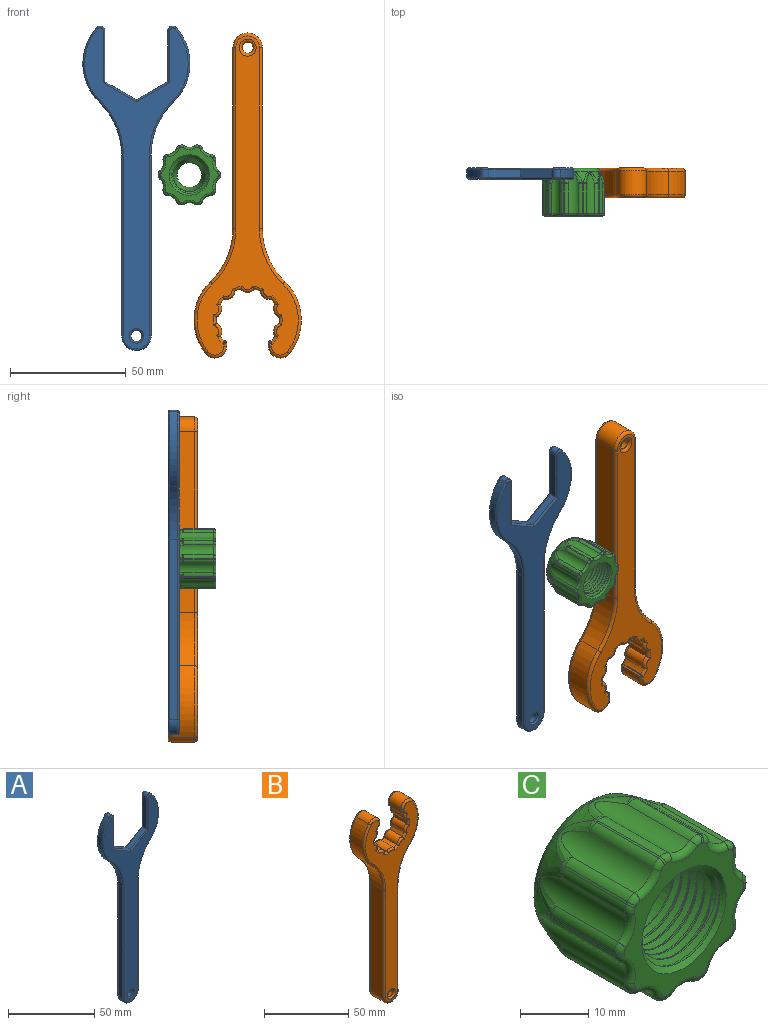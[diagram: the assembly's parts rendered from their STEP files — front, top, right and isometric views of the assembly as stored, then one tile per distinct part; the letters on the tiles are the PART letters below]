
ASSEMBLY  parts=3 mates=2
PART A: 44 faces, bbox 50x4.8x141.1 mm
  f0: cylinder r=6.35mm len=12.7mm, axis (0,1,0), area 64.9mm2, adj f9,f10,f24,f30
  f1: cylinder r=23.09mm len=32.12mm, axis (0,-1,0), area 115.6mm2, adj f12,f14,f27,f36
  f2: plane 21.98x3.25mm, normal (-1,0,0), area 71.5mm2, adj f6,f14,f23,f40
  f3: cylinder r=23.09mm len=32.12mm, axis (0,-1,0), area 115.6mm2, adj f11,f15,f18,f35
  f4: plane 21.98x3.25mm, normal (1,0,0), area 71.5mm2, adj f5,f15,f17,f39
  f5: plane 13.56x7.83mm, normal (0.5,0,0.87), area 50.9mm2, adj f4,f6,f19,f41
  f6: plane 13.56x7.83mm, normal (-0.5,0,0.87), area 50.9mm2, adj f2,f5,f21,f42
  f7: plane 138.45x44.65mm, normal (0,1,0), area 1775mm2, adj f30,f31,f32,f33,f34,f35,f36,f37
  f8: plane 138.45x44.65mm, normal (0,-1,0), area 1775mm2, adj f16,f17,f18,f19,f20,f21,f22,f23
  f9: plane 78.01x3.25mm, normal (1,0,0), area 253.6mm2, adj f0,f12,f26,f32
  f10: plane 78.01x3.25mm, normal (-1,0,0), area 253.6mm2, adj f0,f11,f22,f31
  f11: cylinder r=31.75mm len=22.84mm, axis (0,-1,0), area 82.9mm2, adj f3,f10,f20,f33
  f12: cylinder r=31.75mm len=22.84mm, axis (0,-1,0), area 82.9mm2, adj f1,f9,f28,f34
  f13: cylinder r=2.39mm len=4.78mm, axis (0,1,0), area 48.8mm2, adj f29,f43
  f14: cylinder r=2.03mm len=3.54mm, axis (0,-1,0), area 15.9mm2, adj f1,f2,f25,f38
  f15: cylinder r=2.03mm len=3.54mm, axis (0,-1,0), area 15.9mm2, adj f3,f4,f16,f37
  f16: torus R=1.27mm, axis (0,1,0), area 5.1mm2, adj f8,f15,f17,f18
  f17: cylinder r=0.76mm len=22.42mm, axis (0,0,-1), area 26.5mm2, adj f4,f8,f16,f19
  f18: torus R=22.33mm, axis (0,1,0), area 42mm2, adj f3,f8,f16,f20
  f19: cylinder r=0.76mm len=14.71mm, axis (0.87,0,-0.5), area 19.1mm2, adj f5,f8,f17,f21
  f20: torus R=32.51mm, axis (0,1,0), area 30.8mm2, adj f8,f11,f18,f22
  f21: cylinder r=0.76mm len=14.71mm, axis (0.87,0,0.5), area 19.1mm2, adj f6,f8,f19,f23
  f22: cylinder r=0.76mm len=78.01mm, axis (0,0,-1), area 93.4mm2, adj f8,f10,f20,f24
  f23: cylinder r=0.76mm len=22.42mm, axis (0,0,1), area 26.5mm2, adj f2,f8,f21,f25
  f24: torus R=5.59mm, axis (0,1,0), area 22.8mm2, adj f0,f8,f22,f26
  f25: torus R=1.27mm, axis (0,1,0), area 5.1mm2, adj f8,f14,f23,f27
  f26: cylinder r=0.76mm len=78.01mm, axis (0,0,1), area 93.4mm2, adj f8,f9,f24,f28
  f27: torus R=22.33mm, axis (0,1,0), area 42mm2, adj f1,f8,f25,f28
  f28: torus R=32.51mm, axis (0,1,0), area 30.8mm2, adj f8,f12,f26,f27
  f29: torus R=3.15mm, axis (0,1,0), area 20mm2, adj f8,f13
  f30: torus R=5.59mm, axis (0,1,0), area 22.8mm2, adj f0,f7,f31,f32
  f31: cylinder r=0.76mm len=78.01mm, axis (0,0,1), area 93.4mm2, adj f7,f10,f30,f33
  f32: cylinder r=0.76mm len=78.01mm, axis (0,0,-1), area 93.4mm2, adj f7,f9,f30,f34
  f33: torus R=32.51mm, axis (0,1,0), area 30.8mm2, adj f7,f11,f31,f35
  f34: torus R=32.51mm, axis (0,1,0), area 30.8mm2, adj f7,f12,f32,f36
  f35: torus R=22.33mm, axis (0,1,0), area 42mm2, adj f3,f7,f33,f37
  f36: torus R=22.33mm, axis (0,1,0), area 42mm2, adj f1,f7,f34,f38
  f37: torus R=1.27mm, axis (0,1,0), area 5.1mm2, adj f7,f15,f35,f39
  f38: torus R=1.27mm, axis (0,1,0), area 5.1mm2, adj f7,f14,f36,f40
  f39: cylinder r=0.76mm len=22.42mm, axis (0,0,1), area 26.5mm2, adj f4,f7,f37,f41
  f40: cylinder r=0.76mm len=22.42mm, axis (0,0,-1), area 26.5mm2, adj f2,f7,f38,f42
  f41: cylinder r=0.76mm len=14.71mm, axis (-0.87,0,0.5), area 19.1mm2, adj f5,f7,f39,f42
  f42: cylinder r=0.76mm len=14.71mm, axis (-0.87,0,-0.5), area 19.1mm2, adj f6,f7,f40,f41
  f43: torus R=3.15mm, axis (0,1,0), area 20mm2, adj f7,f13
PART B: 95 faces, bbox 50x12.7x141.1 mm
  f0: cylinder r=6.35mm len=12.7mm, axis (0,1,0), area 202.7mm2, adj f28,f29,f59,f90
  f1: cylinder r=23.11mm len=31.01mm, axis (0,-1,0), area 346.2mm2, adj f26,f31,f60,f84
  f2: plane 137.58x43.69mm, normal (0,1,0), area 1709.6mm2, adj f33,f34,f35,f36,f37,f38,f39,f40
  f3: plane 137.58x43.69mm, normal (0,-1,0), area 1709.6mm2, adj f64,f65,f66,f67,f68,f69,f70,f71
  f4: cylinder r=23.11mm len=31.01mm, axis (0,-1,0), area 346.2mm2, adj f27,f30,f53,f91
  f5: cylinder r=13.59mm len=10.16mm, axis (0,-1,0), area 27.1mm2, adj f6,f21,f42,f66
  f6: cylinder r=3.91mm len=10.16mm, axis (0,-1,0), area 66.8mm2, adj f5,f7,f40,f64
  f7: cylinder r=13.59mm len=10.16mm, axis (0,-1,0), area 27.1mm2, adj f6,f8,f38,f65
  f8: cylinder r=3.91mm len=10.16mm, axis (0,-1,0), area 66.8mm2, adj f7,f9,f36,f67
  f9: cylinder r=13.59mm len=10.16mm, axis (0,-1,0), area 27.1mm2, adj f8,f10,f34,f69
  f10: cylinder r=3.91mm len=10.16mm, axis (0,-1,0), area 66.8mm2, adj f9,f11,f33,f71
  f11: cylinder r=13.59mm len=10.16mm, axis (0,-1,0), area 27.1mm2, adj f10,f12,f35,f73
  f12: cylinder r=3.91mm len=10.16mm, axis (0,-1,0), area 66.8mm2, adj f11,f13,f37,f75
  f13: cylinder r=13.59mm len=10.16mm, axis (0,-1,0), area 27.1mm2, adj f12,f14,f39,f77
  f14: cylinder r=3.91mm len=10.16mm, axis (0,-1,0), area 66.8mm2, adj f13,f15,f41,f79
  f15: cylinder r=13.59mm len=10.16mm, axis (0,-1,0), area 27.1mm2, adj f14,f16,f43,f81
  f16: cylinder r=3.91mm len=10.16mm, axis (0,-1,0), area 5.9mm2, adj f15,f25,f45,f83
  f17: cylinder r=3.91mm len=10.16mm, axis (0,-1,0), area 5.9mm2, adj f18,f24,f52,f76
  f18: cylinder r=13.59mm len=10.16mm, axis (0,-1,0), area 27.1mm2, adj f17,f19,f50,f74
  f19: cylinder r=3.91mm len=10.16mm, axis (0,-1,0), area 66.8mm2, adj f18,f20,f48,f72
  f20: cylinder r=13.59mm len=10.16mm, axis (0,-1,0), area 27.1mm2, adj f19,f21,f46,f70
  f21: cylinder r=3.91mm len=10.16mm, axis (0,-1,0), area 66.8mm2, adj f5,f20,f44,f68
  f22: plane 10.16x1.76mm, normal (-1,0,0), area 17.9mm2, adj f24,f26,f56,f80
  f23: plane 10.16x1.76mm, normal (1,0,0), area 17.9mm2, adj f25,f27,f49,f87
  f24: cylinder r=0.51mm len=10.16mm, axis (0,-1,0), area 8.4mm2, adj f17,f22,f54,f78
  f25: cylinder r=0.51mm len=10.16mm, axis (0,-1,0), area 8.4mm2, adj f16,f23,f47,f85
  f26: cylinder r=5.08mm len=10.16mm, axis (0,-1,0), area 127.5mm2, adj f1,f22,f58,f82
  f27: cylinder r=5.08mm len=10.16mm, axis (0,-1,0), area 127.5mm2, adj f4,f23,f51,f89
  f28: plane 78x10.16mm, normal (1,0,0), area 792.5mm2, adj f0,f31,f61,f88
  f29: plane 78x10.16mm, normal (-1,0,0), area 792.5mm2, adj f0,f30,f57,f92
  f30: cylinder r=31.75mm len=22.85mm, axis (0,-1,0), area 259.1mm2, adj f4,f29,f55,f93
  f31: cylinder r=31.75mm len=22.85mm, axis (0,-1,0), area 259.1mm2, adj f1,f28,f62,f86
  f32: cylinder r=2.39mm len=10.16mm, axis (0,1,0), area 152.4mm2, adj f63,f94
  f33: torus R=2.64mm, axis (0,1,0), area 12.6mm2, adj f2,f10,f34,f35
  f34: torus R=14.86mm, axis (0,1,0), area 6.7mm2, adj f2,f9,f33,f36
  f35: torus R=14.86mm, axis (0,1,0), area 6.7mm2, adj f2,f11,f33,f37
  f36: torus R=2.64mm, axis (0,1,0), area 12.6mm2, adj f2,f8,f34,f38
  f37: torus R=2.64mm, axis (0,1,0), area 12.6mm2, adj f2,f12,f35,f39
  f38: torus R=14.86mm, axis (0,1,0), area 6.7mm2, adj f2,f7,f36,f40
  f39: torus R=14.86mm, axis (0,1,0), area 6.7mm2, adj f2,f13,f37,f41
  f40: torus R=2.64mm, axis (0,1,0), area 12.6mm2, adj f2,f6,f38,f42
  f41: torus R=2.64mm, axis (0,1,0), area 12.6mm2, adj f2,f14,f39,f43
  f42: torus R=14.86mm, axis (0,1,0), area 6.7mm2, adj f2,f5,f40,f44
  f43: torus R=14.86mm, axis (0,1,0), area 6.7mm2, adj f2,f15,f41,f45
  f44: torus R=2.64mm, axis (0,1,0), area 12.6mm2, adj f2,f21,f42,f46
  f45: torus R=2.64mm, axis (0,1,0), area 0.9mm2, adj f2,f16,f43,f47
  f46: torus R=14.86mm, axis (0,1,0), area 6.7mm2, adj f2,f20,f44,f48
  f47: bspline ~1.58x1.49mm, area 1.2mm2, adj f25,f45,f49
  f48: torus R=2.64mm, axis (0,1,0), area 12.6mm2, adj f2,f19,f46,f50
  f49: cylinder r=1.27mm len=1.76mm, axis (0,0,-1), area 2.9mm2, adj f2,f23,f47,f51
  f50: torus R=14.86mm, axis (0,1,0), area 6.7mm2, adj f2,f18,f48,f52
  f51: torus R=3.81mm, axis (0,1,0), area 22.8mm2, adj f2,f27,f49,f53
  f52: torus R=2.64mm, axis (0,1,0), area 0.9mm2, adj f2,f17,f50,f54
  f53: torus R=21.84mm, axis (0,1,0), area 66.6mm2, adj f2,f4,f51,f55
  f54: bspline ~1.58x1.49mm, area 1.2mm2, adj f24,f52,f56
  f55: torus R=33.02mm, axis (0,1,0), area 51.6mm2, adj f2,f30,f53,f57
  f56: cylinder r=1.27mm len=1.76mm, axis (0,0,1), area 2.9mm2, adj f2,f22,f54,f58
  f57: cylinder r=1.27mm len=78mm, axis (0,0,1), area 155.6mm2, adj f2,f29,f55,f59
  f58: torus R=3.81mm, axis (0,1,0), area 22.8mm2, adj f2,f26,f56,f60
  f59: torus R=5.08mm, axis (0,1,0), area 36.9mm2, adj f0,f2,f57,f61
  f60: torus R=21.84mm, axis (0,1,0), area 66.6mm2, adj f1,f2,f58,f62
  f61: cylinder r=1.27mm len=78mm, axis (0,0,-1), area 155.6mm2, adj f2,f28,f59,f62
  f62: torus R=33.02mm, axis (0,1,0), area 51.6mm2, adj f2,f31,f60,f61
  f63: torus R=3.66mm, axis (0,1,0), area 35.7mm2, adj f2,f32
  f64: torus R=2.64mm, axis (0,1,0), area 12.6mm2, adj f3,f6,f65,f66
  f65: torus R=14.86mm, axis (0,1,0), area 6.7mm2, adj f3,f7,f64,f67
  f66: torus R=14.86mm, axis (0,1,0), area 6.7mm2, adj f3,f5,f64,f68
  f67: torus R=2.64mm, axis (0,1,0), area 12.6mm2, adj f3,f8,f65,f69
  f68: torus R=2.64mm, axis (0,1,0), area 12.6mm2, adj f3,f21,f66,f70
  f69: torus R=14.86mm, axis (0,1,0), area 6.7mm2, adj f3,f9,f67,f71
  f70: torus R=14.86mm, axis (0,1,0), area 6.7mm2, adj f3,f20,f68,f72
  f71: torus R=2.64mm, axis (0,1,0), area 12.6mm2, adj f3,f10,f69,f73
  f72: torus R=2.64mm, axis (0,1,0), area 12.6mm2, adj f3,f19,f70,f74
  f73: torus R=14.86mm, axis (0,1,0), area 6.7mm2, adj f3,f11,f71,f75
  f74: torus R=14.86mm, axis (0,1,0), area 6.7mm2, adj f3,f18,f72,f76
  f75: torus R=2.64mm, axis (0,1,0), area 12.6mm2, adj f3,f12,f73,f77
  f76: torus R=2.64mm, axis (0,1,0), area 0.9mm2, adj f3,f17,f74,f78
  f77: torus R=14.86mm, axis (0,1,0), area 6.7mm2, adj f3,f13,f75,f79
  f78: bspline ~1.58x1.49mm, area 1.2mm2, adj f24,f76,f80
  f79: torus R=2.64mm, axis (0,1,0), area 12.6mm2, adj f3,f14,f77,f81
  f80: cylinder r=1.27mm len=1.76mm, axis (0,0,-1), area 2.9mm2, adj f3,f22,f78,f82
  f81: torus R=14.86mm, axis (0,1,0), area 6.7mm2, adj f3,f15,f79,f83
  f82: torus R=3.81mm, axis (0,1,0), area 22.8mm2, adj f3,f26,f80,f84
  f83: torus R=2.64mm, axis (0,1,0), area 0.9mm2, adj f3,f16,f81,f85
  f84: torus R=21.84mm, axis (0,1,0), area 66.6mm2, adj f1,f3,f82,f86
  f85: bspline ~1.58x1.49mm, area 1.2mm2, adj f25,f83,f87
  f86: torus R=33.02mm, axis (0,1,0), area 51.6mm2, adj f3,f31,f84,f88
  f87: cylinder r=1.27mm len=1.76mm, axis (0,0,1), area 2.9mm2, adj f3,f23,f85,f89
  f88: cylinder r=1.27mm len=78mm, axis (0,0,1), area 155.6mm2, adj f3,f28,f86,f90
  f89: torus R=3.81mm, axis (0,1,0), area 22.8mm2, adj f3,f27,f87,f91
  f90: torus R=5.08mm, axis (0,1,0), area 36.9mm2, adj f0,f3,f88,f92
  f91: torus R=21.84mm, axis (0,1,0), area 66.6mm2, adj f3,f4,f89,f93
  f92: cylinder r=1.27mm len=78mm, axis (0,0,-1), area 155.6mm2, adj f3,f29,f90,f93
  f93: torus R=33.02mm, axis (0,1,0), area 51.6mm2, adj f3,f30,f91,f92
  f94: torus R=3.66mm, axis (0,1,0), area 35.7mm2, adj f3,f32
PART C: 135 faces, bbox 28.6x21.1x27.8 mm
  f0: cylinder r=13.46mm len=12.87mm, axis (0,-1,0), area 4.8mm2, adj f9,f74,f83,f100
  f1: cylinder r=13.46mm len=12.87mm, axis (0,-1,0), area 4.8mm2, adj f10,f79,f88,f95
  f2: cylinder r=13.46mm len=12.87mm, axis (0,-1,0), area 4.8mm2, adj f11,f84,f89,f103
  f3: cylinder r=13.46mm len=12.87mm, axis (0,-1,0), area 4.8mm2, adj f12,f48,f93,f111
  f4: cylinder r=13.46mm len=12.87mm, axis (0,-1,0), area 4.8mm2, adj f13,f49,f58,f127
  f5: cylinder r=13.46mm len=12.87mm, axis (0,-1,0), area 4.8mm2, adj f14,f44,f53,f119
  f6: cylinder r=13.46mm len=12.87mm, axis (0,-1,0), area 4.8mm2, adj f15,f64,f73,f116
  f7: cylinder r=13.46mm len=12.87mm, axis (0,-1,0), area 4.8mm2, adj f16,f59,f68,f124
  f8: cylinder r=13.46mm len=12.87mm, axis (0,-1,0), area 4.8mm2, adj f17,f54,f63,f132
  f9: torus R=11.18mm, axis (0,1,0), area 0.3mm2, adj f0,f31,f75,f82
  f10: torus R=11.18mm, axis (0,1,0), area 0.3mm2, adj f1,f31,f80,f87
  f11: torus R=11.18mm, axis (0,1,0), area 0.3mm2, adj f2,f31,f85,f90
  f12: torus R=11.18mm, axis (0,1,0), area 0.3mm2, adj f3,f31,f47,f92
  f13: torus R=11.18mm, axis (0,1,0), area 0.3mm2, adj f4,f31,f50,f57
  f14: torus R=11.18mm, axis (0,1,0), area 0.3mm2, adj f5,f31,f45,f52
  f15: torus R=11.18mm, axis (0,1,0), area 0.3mm2, adj f6,f31,f65,f72
  f16: torus R=11.18mm, axis (0,1,0), area 0.3mm2, adj f7,f31,f60,f67
  f17: torus R=11.18mm, axis (0,1,0), area 0.3mm2, adj f8,f31,f55,f62
  f18: plane 16.9x16.9mm, normal (0,1,0), area 26.3mm2, adj f19,f27,f28,f29,f30
  f19: cylinder r=7.22mm len=14.43mm, axis (0,1,0), area 48.6mm2, adj f18,f21,f28,f30
  f20: cone r=8.74mm half-angle=45deg, axis (0,-1,0), area 73.6mm2, adj f21,f24,f28,f29,f30
  f21: cone r=8.74mm half-angle=45deg, axis (0,-1,0), area 1.9mm2, adj f19,f20,f30
  f22: cylinder r=13.46mm len=12.87mm, axis (0,-1,0), area 4.8mm2, adj f32,f69,f78,f108
  f23: plane 19.1x19.1mm, normal (0,1,0), area 171.9mm2, adj f33,f134
  f24: plane 24.89x23.87mm, normal (0,-1,0), area 178.8mm2, adj f20,f94,f95,f96,f97,f98,f99,f100
  f25: cone r=7.05mm half-angle=20deg, axis (0,-1,0), area 196.3mm2, adj f26,f134
  f26: plane 16.46x16.46mm, normal (0,-1,0), area 56.6mm2, adj f25,f27
  f27: cylinder r=8.23mm len=16.46mm, axis (0,1,0), area 247mm2, adj f18,f26
  f28: bspline ~16.15x16.15mm, area 270.5mm2, adj f18,f19,f20,f29
  f29: bspline ~16.15x16.15mm, area 120mm2, adj f18,f20,f28,f30
  f30: bspline ~16.13x16.13mm, area 271.5mm2, adj f18,f19,f20,f21,f29
  f31: cone r=11.15mm half-angle=20deg, axis (0,-1,0), area 132.4mm2, adj f9,f10,f11,f12,f13,f14,f15,f16
  f32: torus R=11.18mm, axis (0,1,0), area 0.3mm2, adj f22,f31,f70,f77
  f33: torus R=9.55mm, axis (0,1,0), area 189.2mm2, adj f23,f31
  f34: cylinder r=3.97mm len=17.19mm, axis (0,-1,0), area 74.6mm2, adj f69,f70,f71,f72,f73,f112
  f35: cylinder r=3.97mm len=17.19mm, axis (0,-1,0), area 74.6mm2, adj f54,f55,f56,f57,f58,f131
  f36: cylinder r=3.97mm len=17.19mm, axis (0,-1,0), area 74.6mm2, adj f59,f60,f61,f62,f63,f128
  f37: cylinder r=3.97mm len=17.19mm, axis (0,-1,0), area 74.6mm2, adj f64,f65,f66,f67,f68,f120
  f38: cylinder r=3.97mm len=17.19mm, axis (0,-1,0), area 74.6mm2, adj f44,f45,f46,f47,f48,f115
  f39: cylinder r=3.97mm len=17.19mm, axis (0,-1,0), area 74.6mm2, adj f49,f50,f51,f52,f53,f123
  f40: cylinder r=3.97mm len=17.19mm, axis (0,-1,0), area 74.6mm2, adj f89,f90,f91,f92,f93,f107
  f41: cylinder r=3.97mm len=17.19mm, axis (0,-1,0), area 74.6mm2, adj f84,f85,f86,f87,f88,f99
  f42: cylinder r=3.97mm len=17.19mm, axis (0,-1,0), area 74.6mm2, adj f79,f80,f81,f82,f83,f96
  f43: cylinder r=3.97mm len=17.19mm, axis (0,-1,0), area 74.6mm2, adj f74,f75,f76,f77,f78,f104
  f44: cylinder r=2.03mm len=12.87mm, axis (0,1,0), area 23.5mm2, adj f5,f38,f45,f117
  f45: bspline ~1.65x1.35mm, area 0.9mm2, adj f14,f38,f44,f46
  f46: bspline ~7.52x6.8mm, area 14.6mm2, adj f31,f38,f45,f47
  f47: bspline ~1.65x1.6mm, area 0.9mm2, adj f12,f38,f46,f48
  f48: cylinder r=2.03mm len=12.87mm, axis (0,1,0), area 23.5mm2, adj f3,f38,f47,f113
  f49: cylinder r=2.03mm len=12.87mm, axis (0,1,0), area 23.5mm2, adj f4,f39,f50,f125
  f50: bspline ~1.77x1.65mm, area 0.9mm2, adj f13,f39,f49,f51
  f51: bspline ~9.3x6.8mm, area 14.6mm2, adj f31,f39,f50,f52
  f52: bspline ~1.77x1.33mm, area 0.9mm2, adj f14,f39,f51,f53
  f53: cylinder r=2.03mm len=12.87mm, axis (0,1,0), area 23.5mm2, adj f5,f39,f52,f121
  f54: cylinder r=2.03mm len=12.87mm, axis (0,1,0), area 23.5mm2, adj f8,f35,f55,f133
  f55: bspline ~1.65x1.6mm, area 0.9mm2, adj f17,f35,f54,f56
  f56: bspline ~7.32x6.8mm, area 14.6mm2, adj f31,f35,f55,f57
  f57: bspline ~1.35x1.33mm, area 0.9mm2, adj f13,f35,f56,f58
  f58: cylinder r=2.03mm len=12.87mm, axis (0,1,0), area 23.5mm2, adj f4,f35,f57,f129
  f59: cylinder r=2.03mm len=12.87mm, axis (0,1,0), area 23.5mm2, adj f7,f36,f60,f126
  f60: bspline ~1.65x1.6mm, area 0.9mm2, adj f16,f36,f59,f61
  f61: bspline ~8.46x6.8mm, area 14.6mm2, adj f31,f36,f60,f62
  f62: bspline ~1.77x1.33mm, area 0.9mm2, adj f17,f36,f61,f63
  f63: cylinder r=2.03mm len=12.87mm, axis (0,1,0), area 23.5mm2, adj f8,f36,f62,f130
  f64: cylinder r=2.03mm len=12.87mm, axis (0,1,0), area 23.5mm2, adj f6,f37,f65,f118
  f65: bspline ~1.77x1.65mm, area 0.9mm2, adj f15,f37,f64,f66
  f66: bspline ~8.24x6.8mm, area 14.6mm2, adj f31,f37,f65,f67
  f67: bspline ~1.65x1.6mm, area 0.9mm2, adj f16,f37,f66,f68
  f68: cylinder r=2.03mm len=12.87mm, axis (0,1,0), area 23.5mm2, adj f7,f37,f67,f122
  f69: cylinder r=2.03mm len=12.87mm, axis (0,1,0), area 23.5mm2, adj f22,f34,f70,f110
  f70: bspline ~1.65x1.35mm, area 0.9mm2, adj f32,f34,f69,f71
  f71: bspline ~7.32x6.8mm, area 14.6mm2, adj f31,f34,f70,f72
  f72: bspline ~1.6x1.33mm, area 0.9mm2, adj f15,f34,f71,f73
  f73: cylinder r=2.03mm len=12.87mm, axis (0,1,0), area 23.5mm2, adj f6,f34,f72,f114
  f74: cylinder r=2.03mm len=12.87mm, axis (0,1,0), area 23.5mm2, adj f0,f43,f75,f102
  f75: bspline ~1.77x1.65mm, area 0.9mm2, adj f9,f43,f74,f76
  f76: bspline ~9.3x6.8mm, area 14.6mm2, adj f31,f43,f75,f77
  f77: bspline ~1.77x1.33mm, area 0.9mm2, adj f32,f43,f76,f78
  f78: cylinder r=2.03mm len=12.87mm, axis (0,1,0), area 23.5mm2, adj f22,f43,f77,f106
  f79: cylinder r=2.03mm len=12.87mm, axis (0,1,0), area 23.5mm2, adj f1,f42,f80,f94
  f80: bspline ~1.65x1.6mm, area 0.9mm2, adj f10,f42,f79,f81
  f81: bspline ~7.52x6.8mm, area 14.6mm2, adj f31,f42,f80,f82
  f82: bspline ~1.35x1.33mm, area 0.9mm2, adj f9,f42,f81,f83
  f83: cylinder r=2.03mm len=12.87mm, axis (0,1,0), area 23.5mm2, adj f0,f42,f82,f98
  f84: cylinder r=2.03mm len=12.87mm, axis (0,1,0), area 23.5mm2, adj f2,f41,f85,f101
  f85: bspline ~1.65x1.6mm, area 0.9mm2, adj f11,f41,f84,f86
  f86: bspline ~8.84x6.8mm, area 14.6mm2, adj f31,f41,f85,f87
  f87: bspline ~1.77x1.33mm, area 0.9mm2, adj f10,f41,f86,f88
  f88: cylinder r=2.03mm len=12.87mm, axis (0,1,0), area 23.5mm2, adj f1,f41,f87,f97
  f89: cylinder r=2.03mm len=12.87mm, axis (0,1,0), area 23.5mm2, adj f2,f40,f90,f105
  f90: bspline ~1.6x1.33mm, area 0.9mm2, adj f11,f40,f89,f91
  f91: bspline ~8.84x6.8mm, area 14.6mm2, adj f31,f40,f90,f92
  f92: bspline ~1.77x1.65mm, area 0.9mm2, adj f12,f40,f91,f93
  f93: cylinder r=2.03mm len=12.87mm, axis (0,1,0), area 23.5mm2, adj f3,f40,f92,f109
  f94: torus R=1.02mm, axis (0,1,0), area 2.4mm2, adj f24,f79,f95,f96
  f95: torus R=12.45mm, axis (0,1,0), area 0.6mm2, adj f1,f24,f94,f97
  f96: torus R=4.98mm, axis (0,1,0), area 8.3mm2, adj f24,f42,f94,f98
  f97: torus R=1.02mm, axis (0,1,0), area 2.4mm2, adj f24,f88,f95,f99
  f98: torus R=1.02mm, axis (0,1,0), area 2.4mm2, adj f24,f83,f96,f100
  f99: torus R=4.98mm, axis (0,1,0), area 8.3mm2, adj f24,f41,f97,f101
  f100: torus R=12.45mm, axis (0,1,0), area 0.6mm2, adj f0,f24,f98,f102
  f101: torus R=1.02mm, axis (0,1,0), area 2.4mm2, adj f24,f84,f99,f103
  f102: torus R=1.02mm, axis (0,1,0), area 2.4mm2, adj f24,f74,f100,f104
  f103: torus R=12.45mm, axis (0,1,0), area 0.6mm2, adj f2,f24,f101,f105
  f104: torus R=4.98mm, axis (0,1,0), area 8.3mm2, adj f24,f43,f102,f106
  f105: torus R=1.02mm, axis (0,1,0), area 2.4mm2, adj f24,f89,f103,f107
  f106: torus R=1.02mm, axis (0,1,0), area 2.4mm2, adj f24,f78,f104,f108
  f107: torus R=4.98mm, axis (0,1,0), area 8.3mm2, adj f24,f40,f105,f109
  f108: torus R=12.45mm, axis (0,1,0), area 0.6mm2, adj f22,f24,f106,f110
  f109: torus R=1.02mm, axis (0,1,0), area 2.4mm2, adj f24,f93,f107,f111
  f110: torus R=1.02mm, axis (0,1,0), area 2.4mm2, adj f24,f69,f108,f112
  f111: torus R=12.45mm, axis (0,1,0), area 0.6mm2, adj f3,f24,f109,f113
  f112: torus R=4.98mm, axis (0,1,0), area 8.3mm2, adj f24,f34,f110,f114
  f113: torus R=1.02mm, axis (0,1,0), area 2.4mm2, adj f24,f48,f111,f115
  f114: torus R=1.02mm, axis (0,1,0), area 2.4mm2, adj f24,f73,f112,f116
  f115: torus R=4.98mm, axis (0,1,0), area 8.3mm2, adj f24,f38,f113,f117
  f116: torus R=12.45mm, axis (0,1,0), area 0.6mm2, adj f6,f24,f114,f118
  f117: torus R=1.02mm, axis (0,1,0), area 2.4mm2, adj f24,f44,f115,f119
  f118: torus R=1.02mm, axis (0,1,0), area 2.4mm2, adj f24,f64,f116,f120
  f119: torus R=12.45mm, axis (0,1,0), area 0.6mm2, adj f5,f24,f117,f121
  f120: torus R=4.98mm, axis (0,1,0), area 8.3mm2, adj f24,f37,f118,f122
  f121: torus R=1.02mm, axis (0,1,0), area 2.4mm2, adj f24,f53,f119,f123
  f122: torus R=1.02mm, axis (0,1,0), area 2.4mm2, adj f24,f68,f120,f124
  f123: torus R=4.98mm, axis (0,1,0), area 8.3mm2, adj f24,f39,f121,f125
  f124: torus R=12.45mm, axis (0,1,0), area 0.6mm2, adj f7,f24,f122,f126
  f125: torus R=1.02mm, axis (0,1,0), area 2.4mm2, adj f24,f49,f123,f127
  f126: torus R=1.02mm, axis (0,1,0), area 2.4mm2, adj f24,f59,f124,f128
  f127: torus R=12.45mm, axis (0,1,0), area 0.6mm2, adj f4,f24,f125,f129
  f128: torus R=4.98mm, axis (0,1,0), area 8.3mm2, adj f24,f36,f126,f130
  f129: torus R=1.02mm, axis (0,1,0), area 2.4mm2, adj f24,f58,f127,f131
  f130: torus R=1.02mm, axis (0,1,0), area 2.4mm2, adj f24,f63,f128,f132
  f131: torus R=4.98mm, axis (0,1,0), area 8.3mm2, adj f24,f35,f129,f133
  f132: torus R=12.45mm, axis (0,1,0), area 0.6mm2, adj f8,f24,f130,f133
  f133: torus R=1.02mm, axis (0,1,0), area 2.4mm2, adj f24,f54,f131,f132
  f134: torus R=6.04mm, axis (0,1,0), area 50.6mm2, adj f23,f25
PLACE A t=(-85.15,9.74,45.24)mm
PLACE B rot(axis=(0,1,0),180deg) t=(13.6,1.81,-65.41)mm
PLACE C t=(-11.53,-6.12,22.61)mm fixed
MATE planar C.f0 <-> A.f7  axis (0,1,0) through (-11.53,14.51,-2.79)mm
MATE planar B.f2 <-> C.f0  axis (0,1,0) through (28.28,14.51,-63.1)mm
